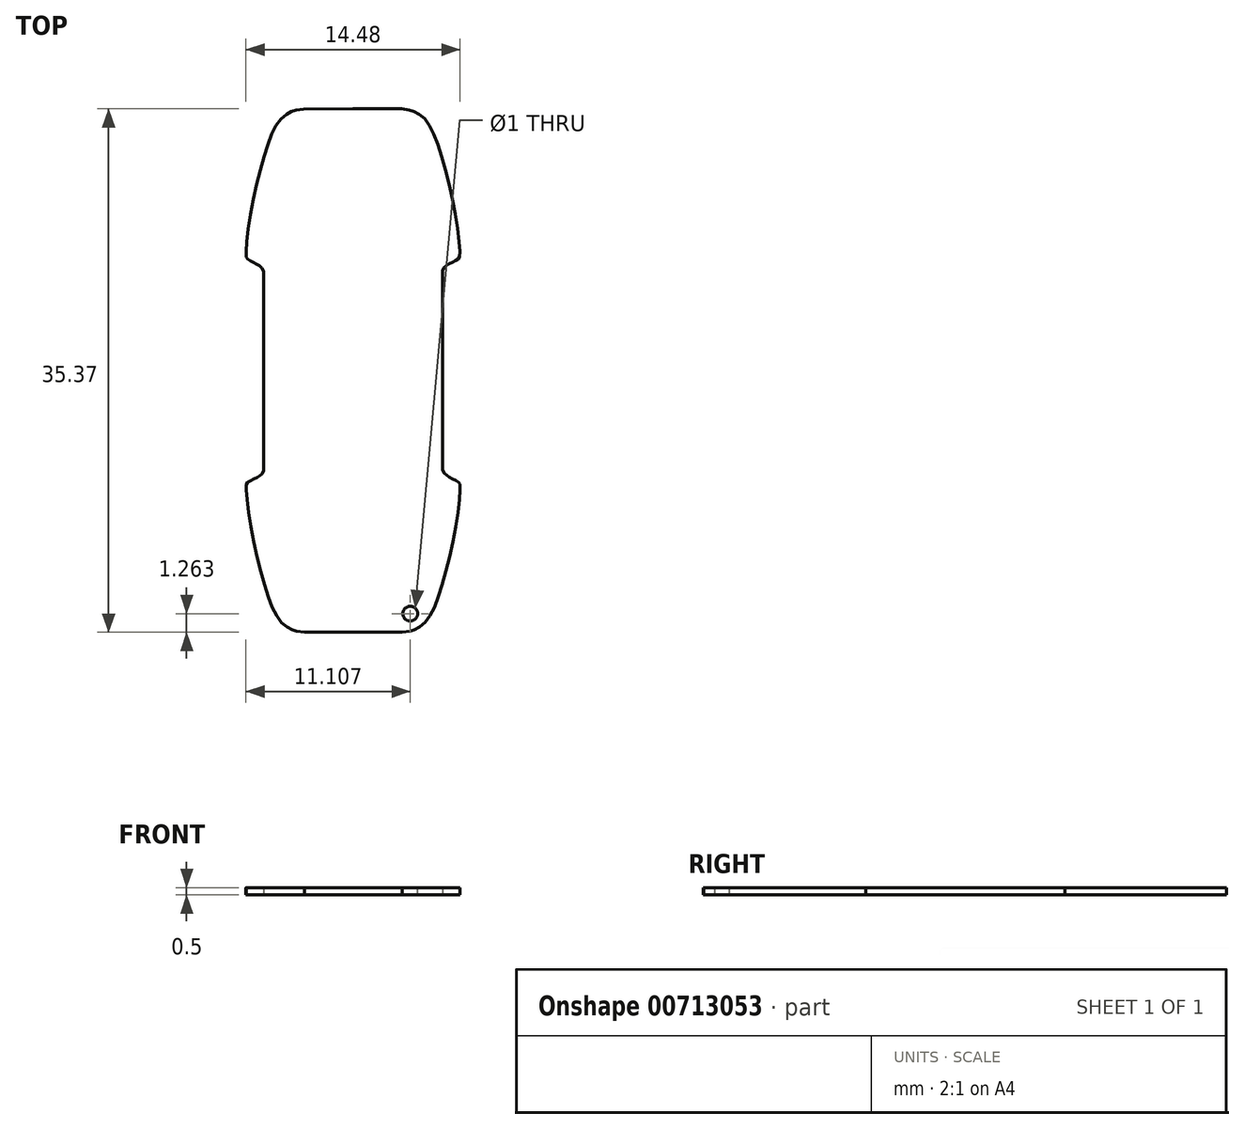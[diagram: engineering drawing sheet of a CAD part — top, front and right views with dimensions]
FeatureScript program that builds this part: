
annotation { "Feature Type Name" : "Feature", "Feature Type Description" : "" }
export const myFeature = defineFeature(function(context is Context, id is Id, definition is map)
    precondition{}
    {
        {
            var Q0;
            Q0=qCreatedBy(makeId("Top.planeOp"),FACE);
            var sketch = newSketch(context, id + "F0", { "sketchPlane" : qUnion([Q0])});
            skFitSpline(sketch, "E0", {"points": [v(8.44, 46.16) * mm, v(9.26, 46) * mm, v(10.02, 45.46) * mm, v(10.94, 43.57) * mm, v(12.04, 39.19) * mm, v(12.37, 36.28) * mm, v(12.32, 36.07) * mm, v(12.17, 35.96) * mm, v(11.95, 35.84) * mm, v(11.68, 35.71) * mm, v(11.48, 35.6) * mm, v(11.31, 35.44) * mm, v(11.2, 35.2) * mm, v(7.7, 10.7) * mm], "startDerivative": vector(25.14, -3.17) * mm, "endDerivative": vector(-22.3, -0.68) * mm});
            skLineSegment(sketch, "E1", {"start": v(5.13, 46.16) * mm, "end": v(8.44, 46.16) * mm});
            skFitSpline(sketch, "E2.MirrorCS", {"points": [v(1.82, 46.15) * mm, v(1, 45.98) * mm, v(0.25, 45.45) * mm, v(-0.67, 43.56) * mm, v(-1.76, 39.17) * mm, v(-2.09, 36.26) * mm, v(-2.03, 36.05) * mm, v(-1.89, 35.95) * mm, v(-1.66, 35.82) * mm, v(-1.4, 35.7) * mm, v(-1.2, 35.58) * mm, v(-1.03, 35.43) * mm, v(-0.9, 35.2) * mm, v(2.64, 10.7) * mm], "startDerivative": vector(-25.13, -3.23) * mm, "endDerivative": vector(22.3, -0.62) * mm});
            skLineSegment(sketch, "E3.MirrorCS", {"start": v(5.13, 46.16) * mm, "end": v(1.82, 46.15) * mm});
            skLineSegment(sketch, "E4.MirrorCS", {"start": v(5.17, 10.79) * mm, "end": v(8.49, 10.8) * mm});
            skFitSpline(sketch, "E5.MirrorCS", {"points": [v(8.49, 10.8) * mm, v(9.3, 10.96) * mm, v(10.06, 11.5) * mm, v(10.97, 13.39) * mm, v(12.07, 17.78) * mm, v(12.39, 20.68) * mm, v(12.33, 20.9) * mm, v(12.2, 21) * mm, v(11.97, 21.13) * mm, v(11.7, 21.25) * mm, v(11.5, 21.37) * mm, v(11.33, 21.52) * mm, v(11.2, 21.75) * mm, v(7.66, 46.25) * mm], "startDerivative": vector(25.13, 3.23) * mm, "endDerivative": vector(-22.3, 0.62) * mm});
            skFitSpline(sketch, "E6.MirrorCS", {"points": [v(1.86, 10.79) * mm, v(1.04, 10.95) * mm, v(0.29, 11.48) * mm, v(-0.63, 13.37) * mm, v(-1.74, 17.76) * mm, v(-2.07, 20.66) * mm, v(-2.01, 20.87) * mm, v(-1.87, 20.98) * mm, v(-1.64, 21.1) * mm, v(-1.38, 21.23) * mm, v(-1.18, 21.35) * mm, v(-1.01, 21.5) * mm, v(-0.89, 21.74) * mm, v(2.6, 46.25) * mm], "startDerivative": vector(-25.14, 3.17) * mm, "endDerivative": vector(22.3, 0.68) * mm});
            skLineSegment(sketch, "E7.MirrorCS", {"start": v(5.17, 10.79) * mm, "end": v(1.86, 10.79) * mm});
            skLineSegment(sketch, "E8", {"start": v(-0.9, 35.2) * mm, "end": v(-0.89, 21.74) * mm});
            skLineSegment(sketch, "E9", {"start": v(11.2, 35.2) * mm, "end": v(11.2, 21.75) * mm});
            skSolve(sketch);
        }
        {
            var Q0;
            Q0 = qSketchRegion(id + "F0", true);
            extrude(context, id + "F1", {"entities" : qUnion([Q0]), "depth" : 0.5 * mm, "offsetDistance" : 25 * mm});
        }
        {
            var Q0;
            Q0=makeQuery(id+"F1.opExtrude","CAP_FACE",FACE,{"disambiguationData":[OSD([sQuery(id+"F0.wireOp",EDGE,"E0"),sQuery(id+"F0.wireOp",EDGE,"E1"),sQuery(id+"F0.wireOp",EDGE,"E2.MirrorCS"),sQuery(id+"F0.wireOp",EDGE,"E3.MirrorCS"),sQuery(id+"F0.wireOp",EDGE,"E4.MirrorCS"),sQuery(id+"F0.wireOp",EDGE,"E5.MirrorCS"),sQuery(id+"F0.wireOp",EDGE,"E6.MirrorCS"),sQuery(id+"F0.wireOp",EDGE,"E7.MirrorCS"),sQuery(id+"F0.wireOp",EDGE,"E8"),sQuery(id+"F0.wireOp",EDGE,"E9")])],"isStart":false});
            var sketch = newSketch(context, id + "F2", { "sketchPlane" : qUnion([Q0])});
            skCircle(sketch, "E10", {"center": v(9.02, 12.05) * mm, "radius": 0.5 * mm});
            skSolve(sketch);
        }
        {
            var Q0;
            Q0 = qSketchRegion(id + "F2", true);
            extrude(context, id + "F3", {"entities" : qUnion([Q0]), "operationType" : NewBodyOperationType.REMOVE, "oppositeDirection" : true, "depth" : 25 * mm, "offsetDistance" : 25 * mm});
        }
    });
